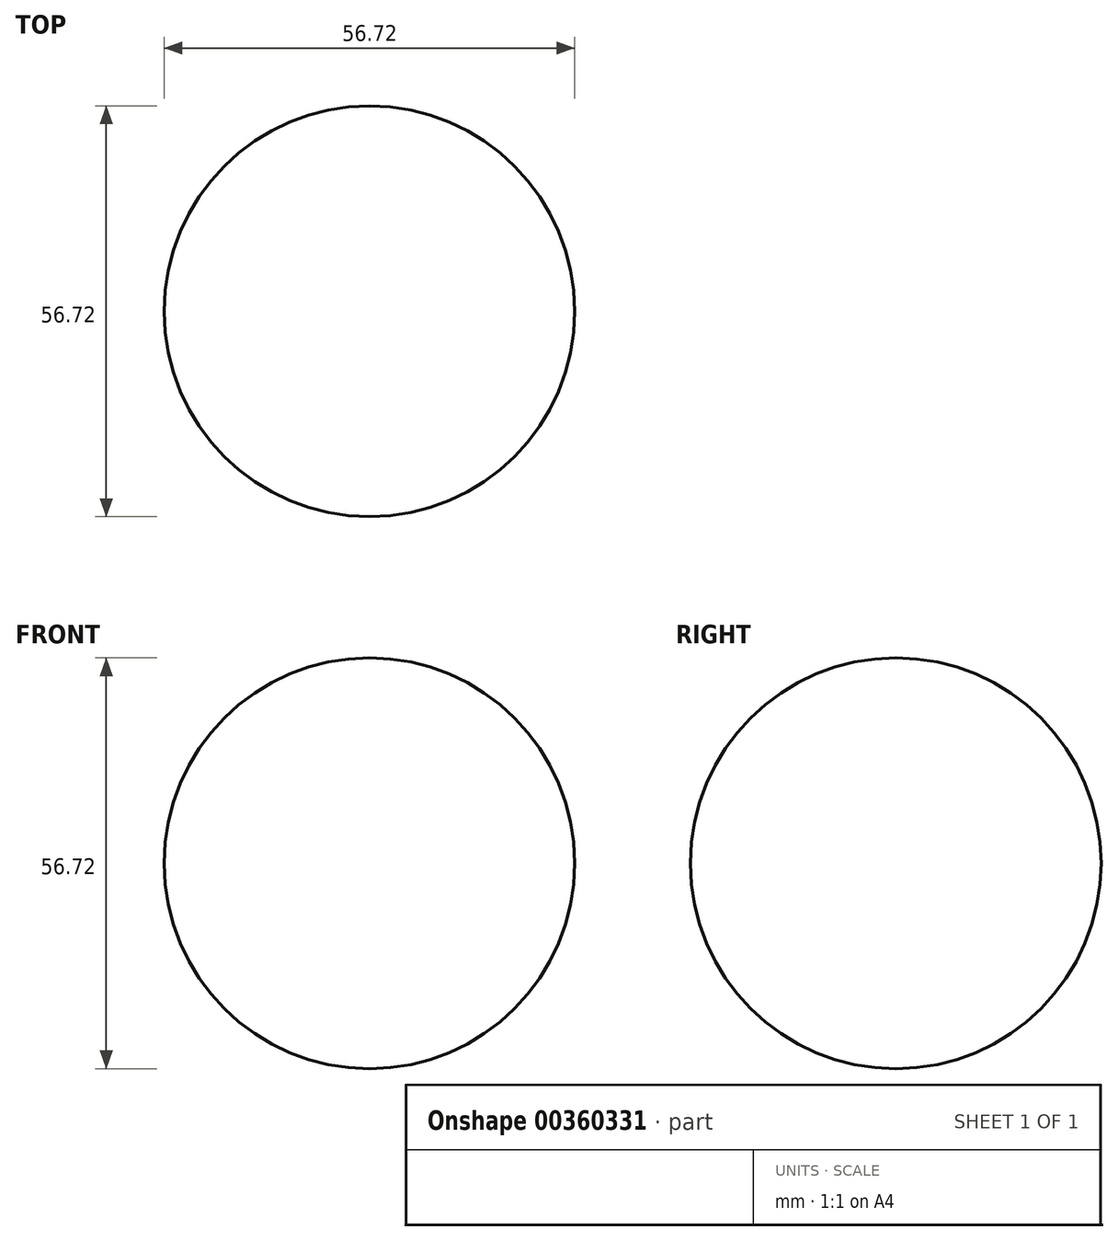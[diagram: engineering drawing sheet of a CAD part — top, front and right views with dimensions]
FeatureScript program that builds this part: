
annotation { "Feature Type Name" : "Feature", "Feature Type Description" : "" }
export const myFeature = defineFeature(function(context is Context, id is Id, definition is map)
    precondition{}
    {
        {
            var Q0;
            Q0=qCreatedBy(makeId("Front.planeOp"),FACE);
            var sketch = newSketch(context, id + "F0", { "sketchPlane" : qUnion([Q0])});
            skArc(sketch, "E0", {"start": v(0, 28.36) * mm, "mid": v(-28.36, 0) * mm, "end": v(0, -28.36) * mm});
            skLineSegment(sketch, "E1", {"start": v(0, 28.36) * mm, "end": v(0, -28.36) * mm});
            skSolve(sketch);
        }
        {
            var Q0;
            Q0=makeQuery(id+"F0.imprint","IMPRINT",FACE,{"disambiguationData":[TD([[makeQuery(id+"F0.imprint","IMPRINT",EDGE,{"derivedFrom":sQuery(id+"F0.wireOp",EDGE,"E0")}),1.0]])]});
            var Q1;
            Q1=sQuery(id+"F0.wireOp",EDGE,"E1");
            revolve(context, id + "F1", {"entities" : qUnion([Q0]), "axis" : qUnion([Q1]), "revolveType" : RevolveType.FULL});
        }
    });
